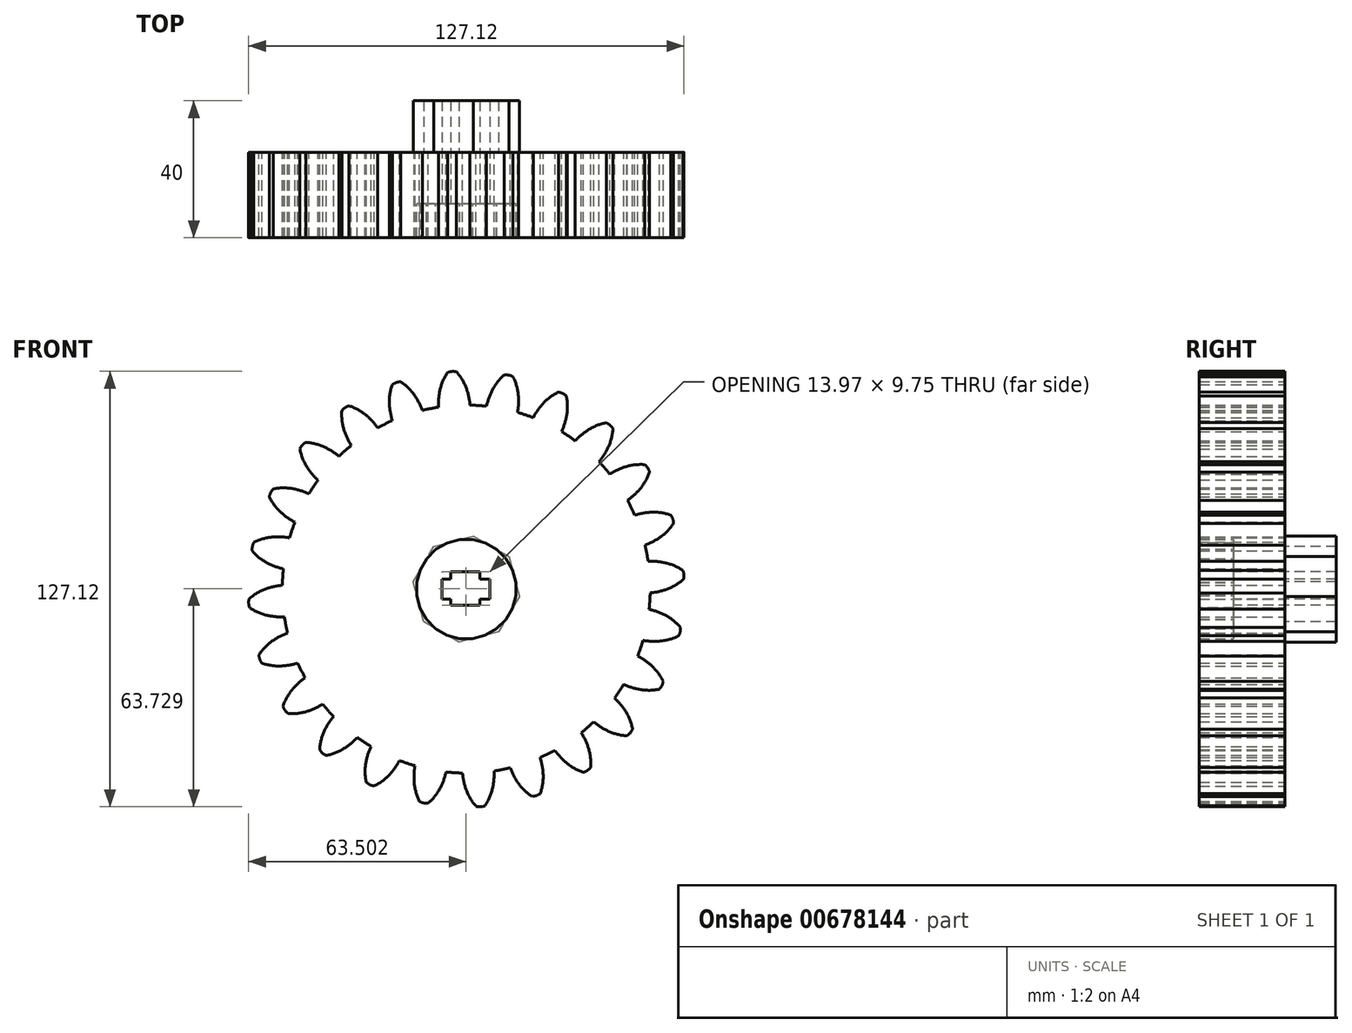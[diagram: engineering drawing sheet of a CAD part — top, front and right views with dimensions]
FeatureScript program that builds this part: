
annotation { "Feature Type Name" : "Feature", "Feature Type Description" : "" }
export const myFeature = defineFeature(function(context is Context, id is Id, definition is map)
    precondition{}
    {
        {
            var Q0;
            Q0=qCreatedBy(makeId("Front.planeOp"),FACE);
            var sketch = newSketch(context, id + "F0", { "sketchPlane" : qUnion([Q0])});
            skCircle(sketch, "E0", {"center": v(0, 0) * mm, "radius": 53.72 * mm});
            skCircle(sketch, "E1", {"center": v(0, 0) * mm, "radius": 58.67 * mm, "construction": true});
            skCircle(sketch, "E2", {"center": v(0, 0) * mm, "radius": 63.5 * mm, "construction": true});
            skLineSegment(sketch, "E3", {"start": v(0, 0) * mm, "end": v(0, 91.84) * mm, "construction": true});
            skLineSegment(sketch, "E4", {"start": v(0, 0) * mm, "end": v(-7.41, 113.09) * mm, "construction": true});
            skLineSegment(sketch, "E5", {"start": v(0, 58.67) * mm, "end": v(-83.5, 56.59) * mm, "construction": true});
            skLineSegment(sketch, "E6", {"start": v(0, 58.67) * mm, "end": v(-75.39, 29.08) * mm, "construction": true});
            skCircle(sketch, "E7", {"center": v(0, 0) * mm, "radius": 54.62 * mm, "construction": true});
            skCircle(sketch, "E8", {"center": v(0, 58.67) * mm, "radius": 16.52 * mm, "construction": true});
            skCircle(sketch, "E9", {"center": v(-15.38, 52.64) * mm, "radius": 16.52 * mm, "construction": true});
            skArc(sketch, "E10", {"start": v(0, 58.67) * mm, "mid": v(-1.21, 61.19) * mm, "end": v(-2.87, 63.43) * mm});
            skArc(sketch, "E11", {"start": v(1.1, 53.7) * mm, "mid": v(0.72, 56.23) * mm, "end": v(0, 58.67) * mm});
            skArc(sketch, "E12.MirrorCS", {"start": v(-8.1, 53.1) * mm, "mid": v(-8.06, 55.65) * mm, "end": v(-7.66, 58.17) * mm});
            skArc(sketch, "E13.MirrorCS", {"start": v(-7.66, 58.17) * mm, "mid": v(-6.78, 60.82) * mm, "end": v(-5.43, 63.27) * mm});
            skArc(sketch, "E14", {"start": v(-2.87, 63.43) * mm, "mid": v(-4.17, 63.55) * mm, "end": v(-5.43, 63.27) * mm});
            skCircle(sketch, "E15.cCircle", {"center": v(0, 0) * mm, "radius": 14.46 * mm, "construction": true});
            skLineSegment(sketch, "E15.0", {"start": v(-15.51, 2.1) * mm, "end": v(-9.48, 12.46) * mm});
            skLineSegment(sketch, "E15.1", {"start": v(-9.48, 12.46) * mm, "end": v(2.1, 15.51) * mm});
            skLineSegment(sketch, "E15.2", {"start": v(2.1, 15.51) * mm, "end": v(12.46, 9.48) * mm});
            skLineSegment(sketch, "E15.3", {"start": v(12.46, 9.48) * mm, "end": v(15.51, -2.1) * mm});
            skLineSegment(sketch, "E15.4", {"start": v(15.51, -2.1) * mm, "end": v(9.48, -12.46) * mm});
            skLineSegment(sketch, "E15.5", {"start": v(9.48, -12.46) * mm, "end": v(-2.1, -15.51) * mm});
            skLineSegment(sketch, "E15.6", {"start": v(-2.1, -15.51) * mm, "end": v(-12.46, -9.48) * mm});
            skLineSegment(sketch, "E15.7", {"start": v(-12.46, -9.48) * mm, "end": v(-15.51, 2.1) * mm});
            skPoint(sketch, "E15.0.midPoint", {"position": v(-12.5, 7.28) * mm});
            skLineSegment(sketch, "E16.bottom", {"start": v(-4.6, 5.04) * mm, "end": v(4, 5.04) * mm});
            skLineSegment(sketch, "E16.top", {"start": v(-4.6, -4.7) * mm, "end": v(4, -4.7) * mm});
            skLineSegment(sketch, "E16.left", {"start": v(-4.6, 5.04) * mm, "end": v(-4.6, -4.7) * mm});
            skLineSegment(sketch, "E16.right", {"start": v(4, 5.04) * mm, "end": v(4, -4.7) * mm});
            skLineSegment(sketch, "E17.bottom", {"start": v(-7.04, 2.93) * mm, "end": v(6.93, 2.93) * mm});
            skLineSegment(sketch, "E17.top", {"start": v(-7.04, -2.92) * mm, "end": v(6.93, -2.92) * mm});
            skLineSegment(sketch, "E17.left", {"start": v(-7.04, 2.93) * mm, "end": v(-7.04, -2.92) * mm});
            skLineSegment(sketch, "E17.right", {"start": v(6.93, 2.93) * mm, "end": v(6.93, -2.92) * mm});
            skSolve(sketch);
        }
        {
            var Q0;
            {var subQ0=sQuery(id+"F0.wireOp",EDGE,"E0");var subQ1=makeQuery(id+"F0.imprint","INTERSECT",VERTEX,{"derivedFrom":[subQ0,sQuery(id+"F0.wireOp",EDGE,"E11")]});Q0=makeQuery(id+"F0.imprint","IMPRINT",FACE,{"disambiguationData":[TD([[makeQuery(id+"F0.imprint","IMPRINT",EDGE,{"disambiguationData":[TD([[subQ1,-1.0]])],"derivedFrom":subQ0}),1.0]])]});}
            var Q1;
            Q1=makeQuery(id+"F0.imprint","IMPRINT",FACE,{"disambiguationData":[TD([[makeQuery(id+"F0.imprint","IMPRINT",EDGE,{"derivedFrom":sQuery(id+"F0.wireOp",EDGE,"E10")}),1.0]])]});
            extrude(context, id + "F1", {"entities" : qUnion([Q0, Q1]), "depth" : 25 * mm, "offsetDistance" : 25 * mm});
        }
        {
            var Q0;
            Q0=makeQuery(id+"F1.opExtrude","SWEPT_BODY",BODY,{"disambiguationData":[OSD([sQuery(id+"F0.wireOp",EDGE,"E0"),sQuery(id+"F0.wireOp",EDGE,"E10"),sQuery(id+"F0.wireOp",EDGE,"E11"),sQuery(id+"F0.wireOp",EDGE,"E12.MirrorCS"),sQuery(id+"F0.wireOp",EDGE,"E13.MirrorCS"),sQuery(id+"F0.wireOp",EDGE,"E14")])]});
            var Q1;
            Q1=makeQuery(id+"F1.opExtrude","SWEPT_FACE",FACE,{"disambiguationData":[OSD([sQuery(id+"F0.wireOp",EDGE,"E0")])]});
            circularPattern(context, id + "F2", {"entities" : qUnion([Q0]), "axis" : qUnion([Q1]), "angle" : 360 * degree, "instanceCount" : 24, "equalSpace" : true});
        }
        {
            var Q0;
            Q0=makeQuery(id+"F0.imprint","IMPRINT",FACE,{"disambiguationData":[TD([[makeQuery(id+"F0.imprint","IMPRINT",EDGE,{"derivedFrom":sQuery(id+"F0.wireOp",EDGE,"E15.0")}),-1.0]])]});
            extrude(context, id + "F3", {"entities" : qUnion([Q0]), "operationType" : NewBodyOperationType.ADD, "endBound" : BoundingType.SYMMETRIC, "oppositeDirection" : true, "depth" : 30 * mm, "offsetDistance" : 25 * mm});
        }
    });
